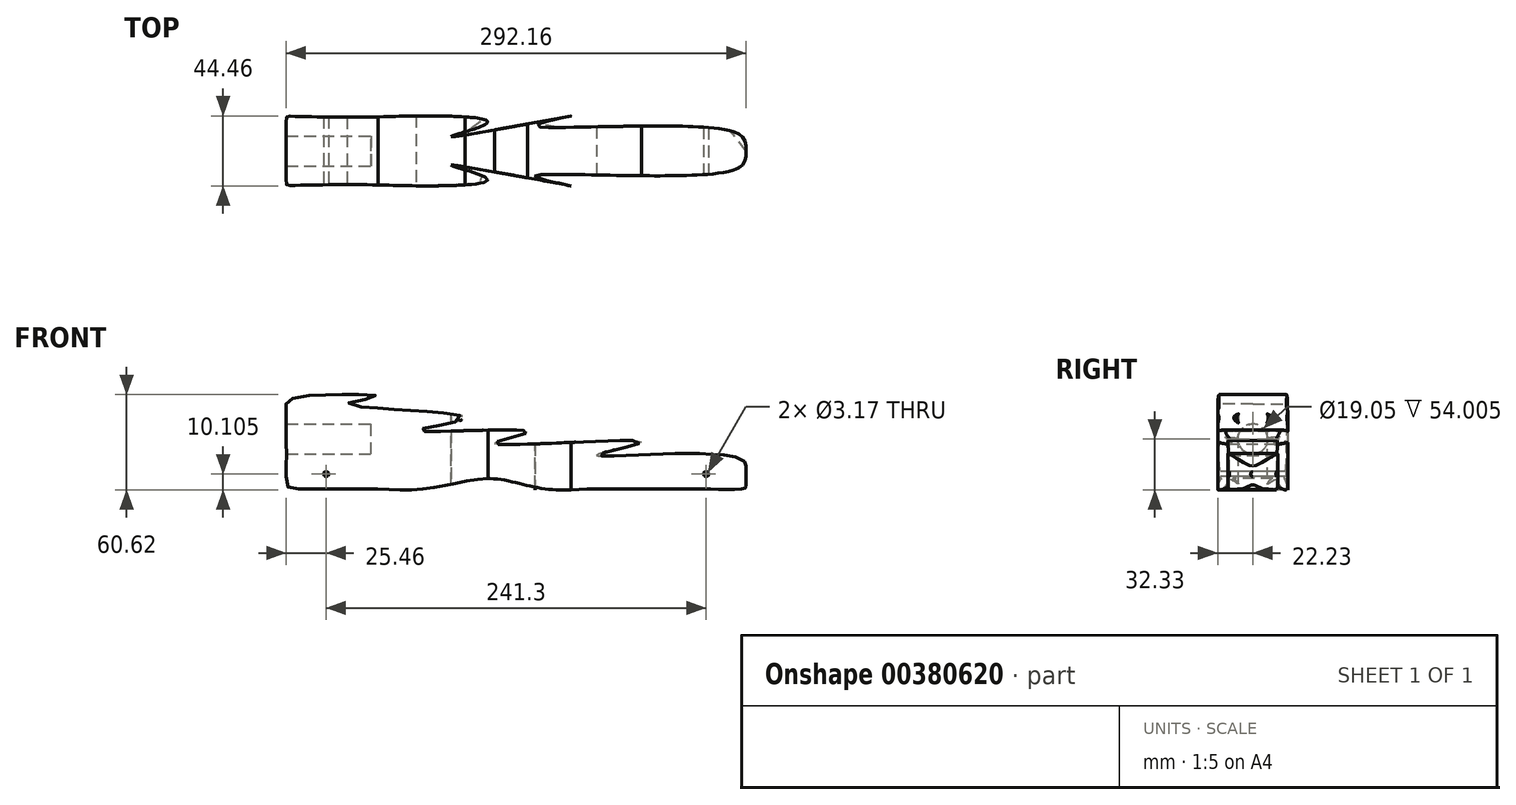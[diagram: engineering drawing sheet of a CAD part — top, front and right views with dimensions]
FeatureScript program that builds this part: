
annotation { "Feature Type Name" : "Feature", "Feature Type Description" : "" }
export const myFeature = defineFeature(function(context is Context, id is Id, definition is map)
    precondition{}
    {
        {
            var Q0;
            Q0=qCreatedBy(makeId("Front.planeOp"),FACE);
            var sketch = newSketch(context, id + "F0", { "sketchPlane" : qUnion([Q0])});
            skLineSegment(sketch, "E0.bottom", {"start": v(-146.05, 31.75) * mm, "end": v(146.05, 31.75) * mm, "construction": true});
            skLineSegment(sketch, "E0.top", {"start": v(-146.05, -31.75) * mm, "end": v(146.05, -31.75) * mm, "construction": true});
            skLineSegment(sketch, "E0.right", {"start": v(146.05, 31.75) * mm, "end": v(146.05, -31.75) * mm, "construction": true});
            skFitSpline(sketch, "E1", {"points": [v(-146.05, -24.02) * mm, v(-146.05, 0) * mm, v(-146.05, 22.4) * mm, v(-142.2, 25.82) * mm, v(-123.91, 28.03) * mm, v(-87.95, 26.84) * mm, v(-107.24, 22.13) * mm, v(-32.55, 13.5) * mm, v(-63.48, 5.3) * mm, v(7.37, 4.66) * mm, v(-13.58, -2.7) * mm, v(79.5, -1.61) * mm, v(51.75, -9.86) * mm, v(81.5, -9.86) * mm, v(127.36, -9.86) * mm, v(144.9, -14.14) * mm, v(146.05, -20.84) * mm, v(146.05, -29.22) * mm, v(145.59, -31.27) * mm, v(144.47, -31.75) * mm, v(115.4, -31.75) * mm, v(90.89, -31.75) * mm, v(68.29, -31.75) * mm, v(46.65, -31.75) * mm, v(19.14, -31.75) * mm, v(-7.68, -26.06) * mm, v(-28.11, -26.06) * mm, v(-58.88, -31.75) * mm, v(-90.58, -31.75) * mm, v(-109.96, -31.75) * mm, v(-137.5, -31.75) * mm, v(-144.78, -30.62) * mm, v(-146.05, -24.02) * mm]});
            skLineSegment(sketch, "E2.bottom", {"start": v(-146.05, 9.52) * mm, "end": v(-95.25, 9.52) * mm, "construction": true});
            skLineSegment(sketch, "E2.top", {"start": v(-141.83, -9.52) * mm, "end": v(-95.25, -9.52) * mm, "construction": true});
            skLineSegment(sketch, "E2.right", {"start": v(-95.25, 9.52) * mm, "end": v(-95.25, -9.52) * mm, "construction": true});
            skLineSegment(sketch, "E3", {"start": v(-146.05, 31.75) * mm, "end": v(-146.05, -31.75) * mm, "construction": true});
            skSolve(sketch);
        }
        {
            var Q0;
            Q0=qCreatedBy(makeId("Top.planeOp"),FACE);
            var sketch = newSketch(context, id + "F1", { "sketchPlane" : qUnion([Q0])});
            skLineSegment(sketch, "E4.bottom", {"start": v(-146.05, 22.22) * mm, "end": v(146.05, 22.23) * mm, "construction": true});
            skLineSegment(sketch, "E4.top", {"start": v(-146.05, -22.23) * mm, "end": v(146.05, -22.22) * mm, "construction": true});
            skLineSegment(sketch, "E4.left", {"start": v(-146.05, 22.22) * mm, "end": v(-146.05, -22.23) * mm, "construction": true});
            skLineSegment(sketch, "E4.right", {"start": v(146.05, 22.22) * mm, "end": v(146.05, -22.22) * mm, "construction": true});
            skLineSegment(sketch, "E5", {"start": v(-146.05, 0) * mm, "end": v(146.05, 0) * mm, "construction": true});
            skFitSpline(sketch, "E6", {"points": [v(-146.05, 0) * mm, v(-146.05, 20.23) * mm, v(-145.64, 21.78) * mm, v(-141.79, 21.98) * mm, v(-93.94, 21.5) * mm, v(-56.49, 22.22) * mm, v(-18.28, 17.71) * mm, v(-41.37, 9.05) * mm, v(34.95, 22.23) * mm, v(12.2, 16.28) * mm, v(134.82, 13.1) * mm, v(146.05, 0) * mm], "startDerivative": vector(0, 442.8) * mm, "endDerivative": vector(0, -277.49) * mm});
            skFitSpline(sketch, "E7.MirrorCS", {"points": [v(-146.05, 0) * mm, v(-146.05, -20.23) * mm, v(-145.64, -21.78) * mm, v(-141.79, -21.98) * mm, v(-93.94, -21.5) * mm, v(-56.49, -22.22) * mm, v(-18.28, -17.71) * mm, v(-41.37, -9.05) * mm, v(34.95, -22.23) * mm, v(12.2, -16.28) * mm, v(134.82, -13.1) * mm, v(146.05, 0) * mm], "startDerivative": vector(0, -442.8) * mm, "endDerivative": vector(0, 277.49) * mm});
            skLineSegment(sketch, "E8.MirrorCS", {"start": v(-146.05, -22.23) * mm, "end": v(146.05, -22.23) * mm});
            skSolve(sketch);
        }
        {
            var Q0;
            Q0=qCreatedBy(makeId("Right.planeOp"),FACE);
            var sketch = newSketch(context, id + "F2", { "sketchPlane" : qUnion([Q0])});
            skCircle(sketch, "E9", {"center": v(0, 0) * mm, "radius": 9.53 * mm});
            skSolve(sketch);
        }
        {
            var Q0;
            Q0=qCreatedBy(makeId("Front.planeOp"),FACE);
            var sketch = newSketch(context, id + "F3", { "sketchPlane" : qUnion([Q0])});
            skCircle(sketch, "E10", {"center": v(-120.65, -22.22) * mm, "radius": 1.59 * mm});
            skCircle(sketch, "E11", {"center": v(120.65, -22.23) * mm, "radius": 1.59 * mm});
            skSolve(sketch);
        }
        {
            var Q0;
            Q0=qSketchRegion(id+"F0",true);
            extrude(context, id + "F4", {"entities" : qUnion([Q0]), "depth" : 44.7 * mm, "symmetric" : true});
        }
        {
            var Q0;
            Q0 = qSketchRegion(id + "F1", true);
            extrude(context, id + "F5", {"entities" : qUnion([Q0]), "operationType" : NewBodyOperationType.INTERSECT, "endBound" : BoundingType.THROUGH_ALL, "oppositeDirection" : true, "depth" : 60.96 * mm, "hasSecondDirection" : true, "secondDirectionBound" : BoundingType.THROUGH_ALL, "secondDirectionOppositeDirection" : false, "secondDirectionDepth" : 25.4 * mm});
        }
        {
            var Q0;
            Q0=qSketchRegion(id+"F2",true);
            extrude(context, id + "F6", {"entities" : qUnion([Q0]), "operationType" : NewBodyOperationType.REMOVE, "oppositeDirection" : true, "depth" : 152.4 * mm, "hasSecondDirection" : true, "secondDirectionOppositeDirection" : true, "secondDirectionDepth" : 92.07 * mm});
        }
        {
            var Q0;
            Q0=qSketchRegion(id+"F3",true);
            extrude(context, id + "F7", {"entities" : qUnion([Q0]), "operationType" : NewBodyOperationType.REMOVE, "oppositeDirection" : true, "depth" : 50.8 * mm, "symmetric" : true});
        }
    });
